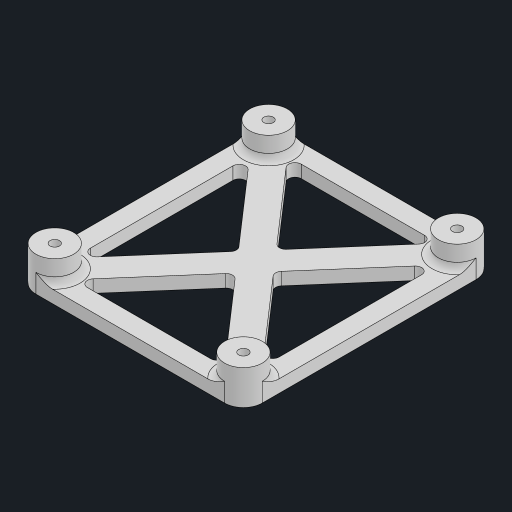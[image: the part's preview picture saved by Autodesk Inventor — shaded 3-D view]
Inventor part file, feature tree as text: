
AUTODESK INVENTOR PART (.ipt)
format: ipt  version: 2023 (Build 270158000, 158)  size: 214,528 bytes
history: native  units: mm
features: sketch x3, projected_geometry x3, extrude x2, fillet x2, other x1, hole x1
ambient origin geometry x8: Origin, YZ Plane, XZ Plane, XY Plane, X Axis, Y Axis, Z Axis, Center Point
bodies: Body1 (feature_tree)
feature tree (12):
  other  "ソリッド1"
  extrude  "押し出し1"  Depth=30.0mm
  extrude  "押し出し2"  Depth=34.0mm
  hole  "穴1"  [1 undecoded]
  fillet  "フィレット1"  Radius=40.0mm
  fillet  "フィレット2"  Radius=2.0mm
  sketch  "スケッチ1"
  sketch  "スケッチ2"
  sketch  "スケッチ3"
  projected_geometry  "投影ループ1"
  projected_geometry  "投影ループ2"
  projected_geometry  "投影ループ3"
note: 1 required parameter value undecoded (feature->parameter linkage not recoverable at this tier; creation-order binding heuristic only, values carry confidence <= 0.55)
